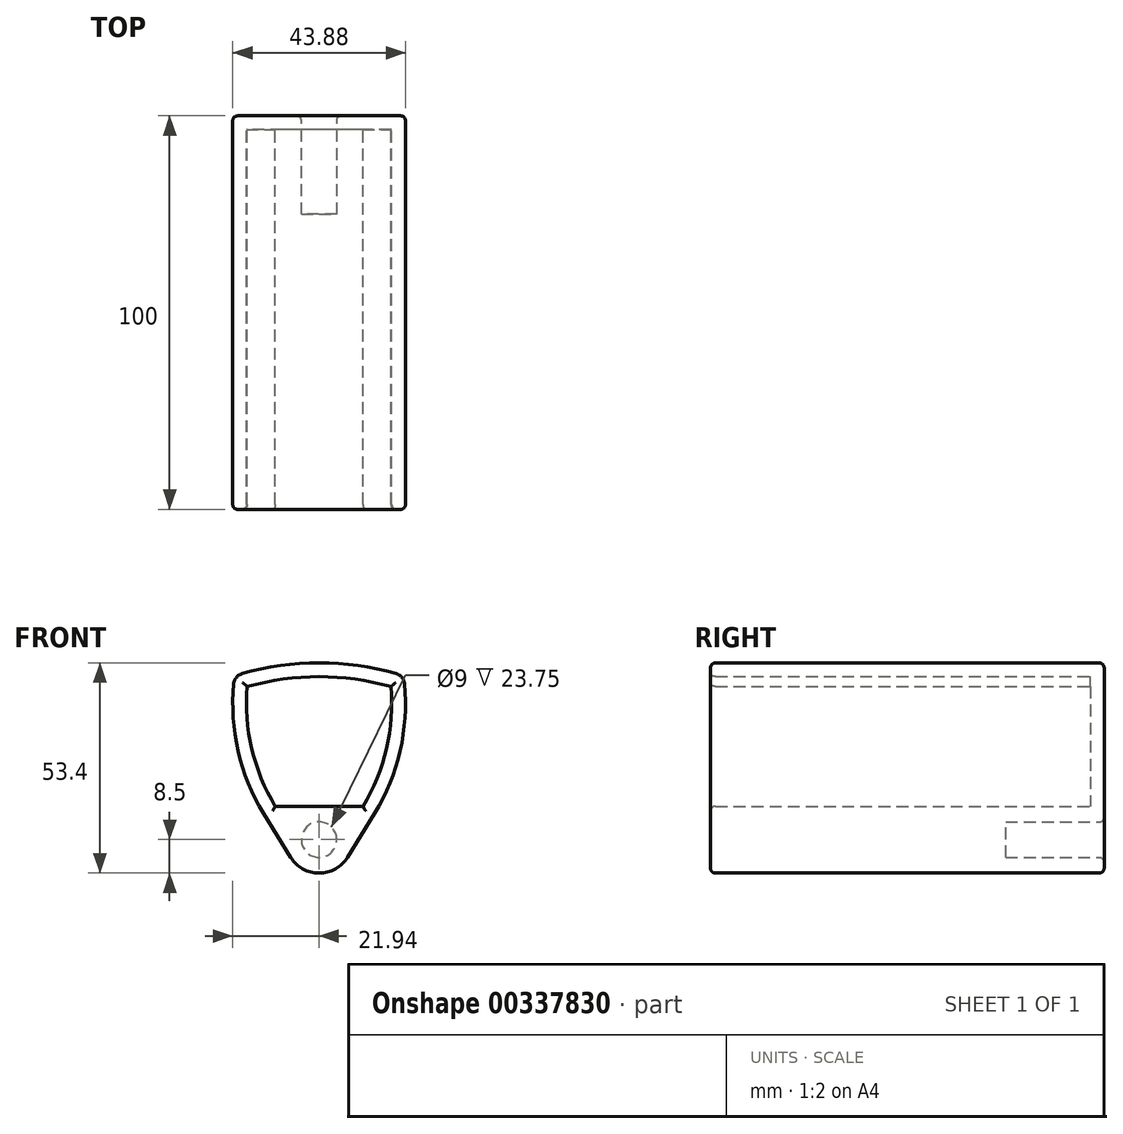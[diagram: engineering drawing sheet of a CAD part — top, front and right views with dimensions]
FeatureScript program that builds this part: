
annotation { "Feature Type Name" : "Feature", "Feature Type Description" : "" }
export const myFeature = defineFeature(function(context is Context, id is Id, definition is map)
    precondition{}
    {
        {
            var Q0;
            Q0=qCreatedBy(makeId("Front.planeOp"),FACE);
            var sketch = newSketch(context, id + "F0", { "sketchPlane" : qUnion([Q0])});
            skLineSegment(sketch, "E0", {"start": v(11.12, 0) * mm, "end": v(-11.12, 0) * mm});
            skArc(sketch, "E1", {"start": v(18.25, 30.4) * mm, "mid": v(0, 32.9) * mm, "end": v(-18.25, 30.4) * mm});
            skArc(sketch, "E2", {"start": v(-18.25, 30.4) * mm, "mid": v(-17.12, 14.63) * mm, "end": v(-11.12, 0) * mm});
            skArc(sketch, "E3", {"start": v(11.13, 0) * mm, "mid": v(17.12, 14.63) * mm, "end": v(18.25, 30.4) * mm});
            skArc(sketch, "E4.0", {"start": v(-21.47, 33.1) * mm, "mid": v(-20.8, 15) * mm, "end": v(-14.11, -1.82) * mm});
            skArc(sketch, "E4.1", {"start": v(21.47, 33.1) * mm, "mid": v(0, 36.4) * mm, "end": v(-21.47, 33.1) * mm});
            skArc(sketch, "E4.2", {"start": v(14.11, -1.82) * mm, "mid": v(20.8, 15) * mm, "end": v(21.47, 33.1) * mm});
            skCircle(sketch, "E5", {"center": v(0, -8.5) * mm, "radius": 4.5 * mm});
            skLineSegment(sketch, "E6", {"start": v(-14.11, -1.82) * mm, "end": v(-7.23, -12.97) * mm});
            skLineSegment(sketch, "E7", {"start": v(7.23, -12.97) * mm, "end": v(14.11, -1.82) * mm});
            skArc(sketch, "E8", {"start": v(-7.23, -12.97) * mm, "mid": v(0, -17) * mm, "end": v(7.23, -12.97) * mm});
            skSolve(sketch);
        }
        {
            var Q0;
            Q0=makeQuery(id+"F0.imprint","IMPRINT",FACE,{"disambiguationData":[TD([[makeQuery(id+"F0.imprint","IMPRINT",EDGE,{"derivedFrom":sQuery(id+"F0.wireOp",EDGE,"E0")}),1.0]])]});
            extrude(context, id + "F1", {"entities" : qUnion([Q0]), "depth" : 100 * mm});
        }
        {
            var Q0;
            Q0=makeQuery(id+"F0.imprint","IMPRINT",FACE,{"disambiguationData":[TD([[makeQuery(id+"F0.imprint","IMPRINT",EDGE,{"derivedFrom":sQuery(id+"F0.wireOp",EDGE,"E0")}),-1.0]])]});
            extrude(context, id + "F2", {"entities" : qUnion([Q0]), "operationType" : NewBodyOperationType.ADD, "depth" : 3.5 * mm});
        }
        {
            var Q0;
            Q0=makeQuery(id+"F0.imprint","IMPRINT",FACE,{"disambiguationData":[TD([[makeQuery(id+"F0.imprint","IMPRINT",EDGE,{"derivedFrom":sQuery(id+"F0.wireOp",EDGE,"E5")}),1.0]])]});
            extrude(context, id + "F3", {"entities" : qUnion([Q0]), "operationType" : NewBodyOperationType.ADD, "depth" : 100 * mm});
        }
        {
            var Q0;
            Q0=makeQuery(id+"F0.imprint","IMPRINT",FACE,{"disambiguationData":[TD([[makeQuery(id+"F0.imprint","IMPRINT",EDGE,{"derivedFrom":sQuery(id+"F0.wireOp",EDGE,"E5")}),1.0]])]});
            extrude(context, id + "F4", {"entities" : qUnion([Q0]), "operationType" : NewBodyOperationType.REMOVE, "depth" : 25 * mm});
        }
        {
            var Q0;
            Q0=makeQuery(id+"F1.opExtrude","SWEPT_EDGE",EDGE,{"disambiguationData":[OSD([sQuery(id+"F0.wireOp",EDGE,"E4.0"),sQuery(id+"F0.wireOp",EDGE,"E4.1")])]});
            var Q1;
            Q1=makeQuery(id+"F1.opExtrude","SWEPT_EDGE",EDGE,{"disambiguationData":[OSD([sQuery(id+"F0.wireOp",EDGE,"E4.1"),sQuery(id+"F0.wireOp",EDGE,"E4.2")])]});
            fillet(context, id + "F5", {"entities" : qUnion([Q0, Q1]), "radius" : 3 * mm, "tangentPropagation" : true, "allowEdgeOverflow" : false});
        }
        {
            var Q0;
            {var subQ0=sQuery(id+"F0.wireOp",EDGE,"E5");Q0=makeQuery(id+"F3.boolean.opBoolean","MERGE",FACE,{"derivedFrom":[makeQuery(id+"F1.opExtrude","CAP_FACE",FACE,{"disambiguationData":[OSD([sQuery(id+"F0.wireOp",EDGE,"E0"),sQuery(id+"F0.wireOp",EDGE,"E1"),sQuery(id+"F0.wireOp",EDGE,"E2"),sQuery(id+"F0.wireOp",EDGE,"E3"),sQuery(id+"F0.wireOp",EDGE,"E4.0"),sQuery(id+"F0.wireOp",EDGE,"E4.1"),sQuery(id+"F0.wireOp",EDGE,"E4.2"),subQ0,sQuery(id+"F0.wireOp",EDGE,"E6"),sQuery(id+"F0.wireOp",EDGE,"E7"),sQuery(id+"F0.wireOp",EDGE,"E8")])],"isStart":false}),makeQuery(id+"F3.opExtrude","CAP_FACE",FACE,{"disambiguationData":[OSD([subQ0])],"isStart":false})]});}
            fillet(context, id + "F6", {"entities" : qUnion([Q0]), "radius" : 1.25 * mm, "tangentPropagation" : true, "allowEdgeOverflow" : false});
        }
        {
            var Q0;
            {var subQ0=sQuery(id+"F0.wireOp",EDGE,"E5");var subQ1=sQuery(id+"F0.wireOp",EDGE,"E3");var subQ2=sQuery(id+"F0.wireOp",EDGE,"E2");var subQ3=sQuery(id+"F0.wireOp",EDGE,"E1");var subQ4=sQuery(id+"F0.wireOp",EDGE,"E0");Q0=makeQuery(id+"F3.boolean.opBoolean","MERGE",FACE,{"derivedFrom":[makeQuery(id+"F2.boolean.opBoolean","MERGE",FACE,{"derivedFrom":[makeQuery(id+"F1.opExtrude","CAP_FACE",FACE,{"disambiguationData":[OSD([subQ4,subQ3,subQ2,subQ1,sQuery(id+"F0.wireOp",EDGE,"E4.0"),sQuery(id+"F0.wireOp",EDGE,"E4.1"),sQuery(id+"F0.wireOp",EDGE,"E4.2"),subQ0,sQuery(id+"F0.wireOp",EDGE,"E6"),sQuery(id+"F0.wireOp",EDGE,"E7"),sQuery(id+"F0.wireOp",EDGE,"E8")])],"isStart":true}),makeQuery(id+"F2.opExtrude","CAP_FACE",FACE,{"disambiguationData":[OSD([subQ4,subQ3,subQ2,subQ1])],"isStart":true})]}),makeQuery(id+"F3.opExtrude","CAP_FACE",FACE,{"disambiguationData":[OSD([subQ0])],"isStart":true})]});}
            fillet(context, id + "F7", {"entities" : qUnion([Q0]), "radius" : 1.25 * mm, "tangentPropagation" : true, "allowEdgeOverflow" : false});
        }
    });
